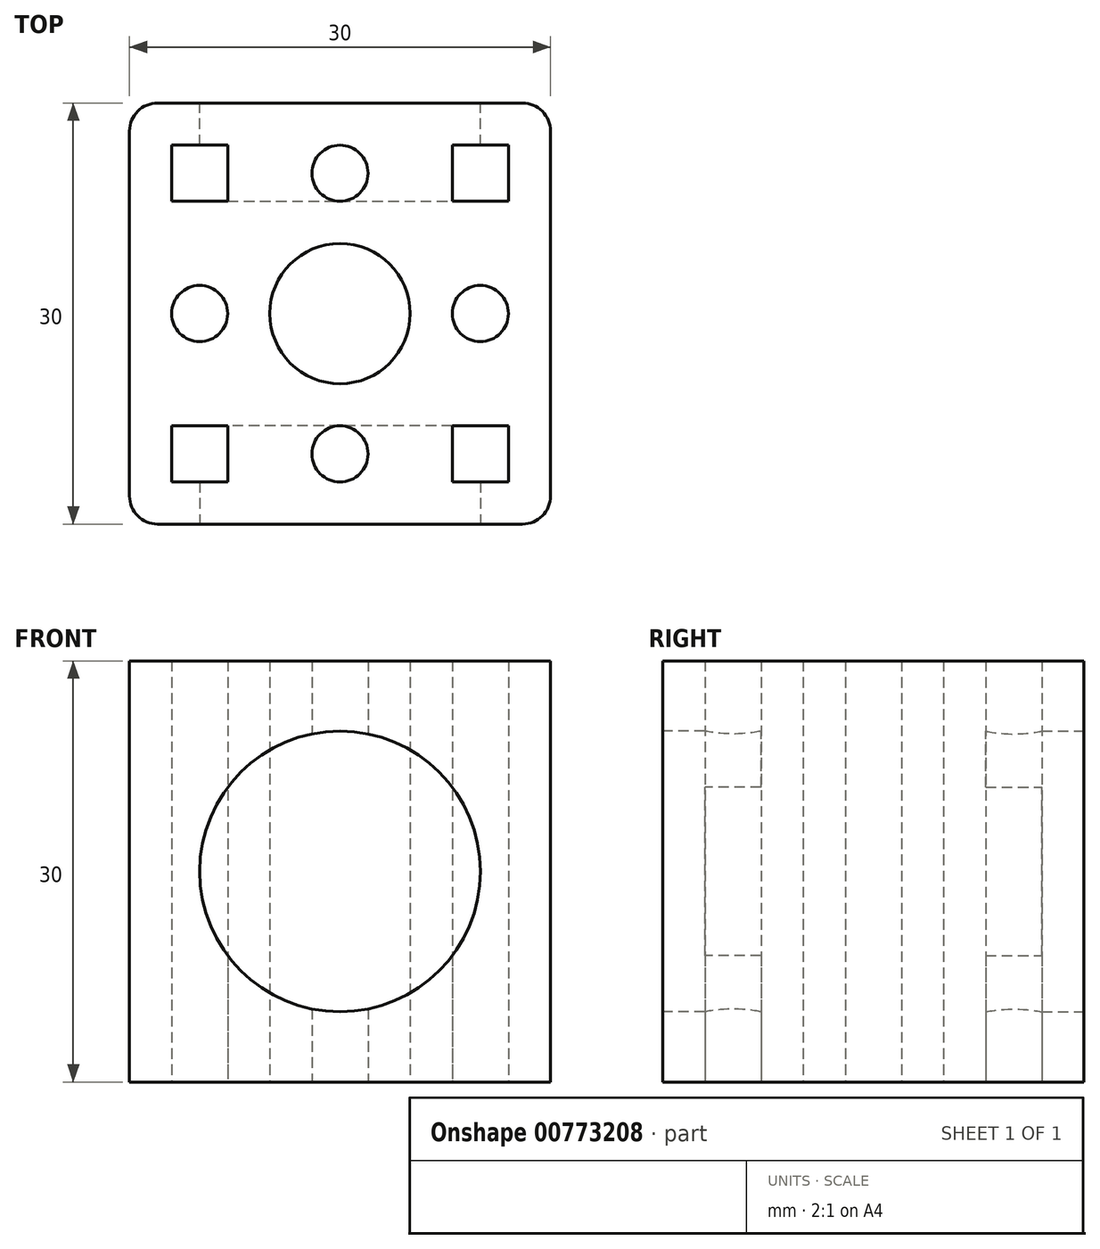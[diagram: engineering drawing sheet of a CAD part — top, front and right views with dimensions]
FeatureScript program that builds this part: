
annotation { "Feature Type Name" : "Feature", "Feature Type Description" : "" }
export const myFeature = defineFeature(function(context is Context, id is Id, definition is map)
    precondition{}
    {
        {
            var Q0;
            Q0=qCreatedBy(makeId("Top.planeOp"),FACE);
            var sketch = newSketch(context, id + "F0", { "sketchPlane" : qUnion([Q0])});
            skLineSegment(sketch, "E0.bottom", {"start": v(15, -15) * mm, "end": v(-15, -15) * mm});
            skLineSegment(sketch, "E0.top", {"start": v(15, 15) * mm, "end": v(-15, 15) * mm});
            skLineSegment(sketch, "E0.left", {"start": v(15, -15) * mm, "end": v(15, 15) * mm});
            skLineSegment(sketch, "E0.right", {"start": v(-15, -15) * mm, "end": v(-15, 15) * mm});
            skPoint(sketch, "E0.middle", {"position": v(0, 0) * mm});
            skCircle(sketch, "E1", {"center": v(0, 10) * mm, "radius": 2 * mm});
            skCircle(sketch, "E2", {"center": v(-10, 0) * mm, "radius": 2 * mm});
            skCircle(sketch, "E3", {"center": v(0, -10) * mm, "radius": 2 * mm});
            skCircle(sketch, "E4", {"center": v(10, 0) * mm, "radius": 2 * mm});
            skCircle(sketch, "E5", {"center": v(0, 0) * mm, "radius": 5 * mm});
            skLineSegment(sketch, "E6.bottom", {"start": v(-12, 12) * mm, "end": v(-8, 12) * mm});
            skLineSegment(sketch, "E6.top", {"start": v(-12, 8) * mm, "end": v(-8, 8) * mm});
            skLineSegment(sketch, "E6.left", {"start": v(-12, 12) * mm, "end": v(-12, 8) * mm});
            skLineSegment(sketch, "E6.right", {"start": v(-8, 12) * mm, "end": v(-8, 8) * mm});
            skLineSegment(sketch, "E7.bottom", {"start": v(8, 12) * mm, "end": v(12, 12) * mm});
            skLineSegment(sketch, "E7.top", {"start": v(8, 8) * mm, "end": v(12, 8) * mm});
            skLineSegment(sketch, "E7.left", {"start": v(8, 12) * mm, "end": v(8, 8) * mm});
            skLineSegment(sketch, "E7.right", {"start": v(12, 12) * mm, "end": v(12, 8) * mm});
            skLineSegment(sketch, "E8.bottom", {"start": v(-8, -8) * mm, "end": v(-12, -8) * mm});
            skLineSegment(sketch, "E8.top", {"start": v(-8, -12) * mm, "end": v(-12, -12) * mm});
            skLineSegment(sketch, "E8.left", {"start": v(-8, -8) * mm, "end": v(-8, -12) * mm});
            skLineSegment(sketch, "E8.right", {"start": v(-12, -8) * mm, "end": v(-12, -12) * mm});
            skLineSegment(sketch, "E9.bottom", {"start": v(12, -8) * mm, "end": v(8, -8) * mm});
            skLineSegment(sketch, "E9.top", {"start": v(12, -12) * mm, "end": v(8, -12) * mm});
            skLineSegment(sketch, "E9.left", {"start": v(12, -8) * mm, "end": v(12, -12) * mm});
            skLineSegment(sketch, "E9.right", {"start": v(8, -8) * mm, "end": v(8, -12) * mm});
            skSolve(sketch);
        }
        {
            var Q0;
            Q0 = qSketchRegion(id + "F0", true);
            extrude(context, id + "F1", {"entities" : qUnion([Q0]), "depth" : 30 * mm, "offsetDistance" : 25 * mm});
        }
        {
            var Q0;
            Q0=makeQuery(id+"F1.opExtrude","SWEPT_EDGE",EDGE,{"disambiguationData":[OSD([sQuery(id+"F0.wireOp",EDGE,"E0.top"),sQuery(id+"F0.wireOp",EDGE,"E0.right")])]});
            var Q1;
            Q1=makeQuery(id+"F1.opExtrude","SWEPT_EDGE",EDGE,{"disambiguationData":[OSD([sQuery(id+"F0.wireOp",EDGE,"E0.bottom"),sQuery(id+"F0.wireOp",EDGE,"E0.right")])]});
            var Q2;
            Q2=makeQuery(id+"F1.opExtrude","SWEPT_EDGE",EDGE,{"disambiguationData":[OSD([sQuery(id+"F0.wireOp",EDGE,"E0.top"),sQuery(id+"F0.wireOp",EDGE,"E0.left")])]});
            var Q3;
            Q3=makeQuery(id+"F1.opExtrude","SWEPT_EDGE",EDGE,{"disambiguationData":[OSD([sQuery(id+"F0.wireOp",EDGE,"E0.bottom"),sQuery(id+"F0.wireOp",EDGE,"E0.left")])]});
            fillet(context, id + "F2", {"entities" : qUnion([Q0, Q1, Q2, Q3]), "radius" : 2 * mm, "tangentPropagation" : true, "allowEdgeOverflow" : false});
        }
        {
            var Q0;
            Q0=makeQuery(id+"F1.opExtrude","SWEPT_FACE",FACE,{"disambiguationData":[OSD([sQuery(id+"F0.wireOp",EDGE,"E0.top")])]});
            var sketch = newSketch(context, id + "F3", { "sketchPlane" : qUnion([Q0])});
            skCircle(sketch, "E10", {"center": v(0, 15) * mm, "radius": 10 * mm});
            skSolve(sketch);
        }
        {
            var Q0;
            Q0 = qSketchRegion(id + "F3", true);
            extrude(context, id + "F4", {"entities" : qUnion([Q0]), "operationType" : NewBodyOperationType.REMOVE, "oppositeDirection" : true, "depth" : 7 * mm, "offsetDistance" : 25 * mm});
        }
        {
            var Q0;
            Q0=makeQuery(id+"F1.opExtrude","SWEPT_FACE",FACE,{"disambiguationData":[OSD([sQuery(id+"F0.wireOp",EDGE,"E0.bottom")])]});
            var sketch = newSketch(context, id + "F5", { "sketchPlane" : qUnion([Q0])});
            skCircle(sketch, "E11", {"center": v(0, 15) * mm, "radius": 10 * mm});
            skSolve(sketch);
        }
        {
            var Q0;
            Q0 = qSketchRegion(id + "F5", true);
            extrude(context, id + "F6", {"entities" : qUnion([Q0]), "operationType" : NewBodyOperationType.REMOVE, "oppositeDirection" : true, "depth" : 7 * mm, "offsetDistance" : 25 * mm});
        }
    });
